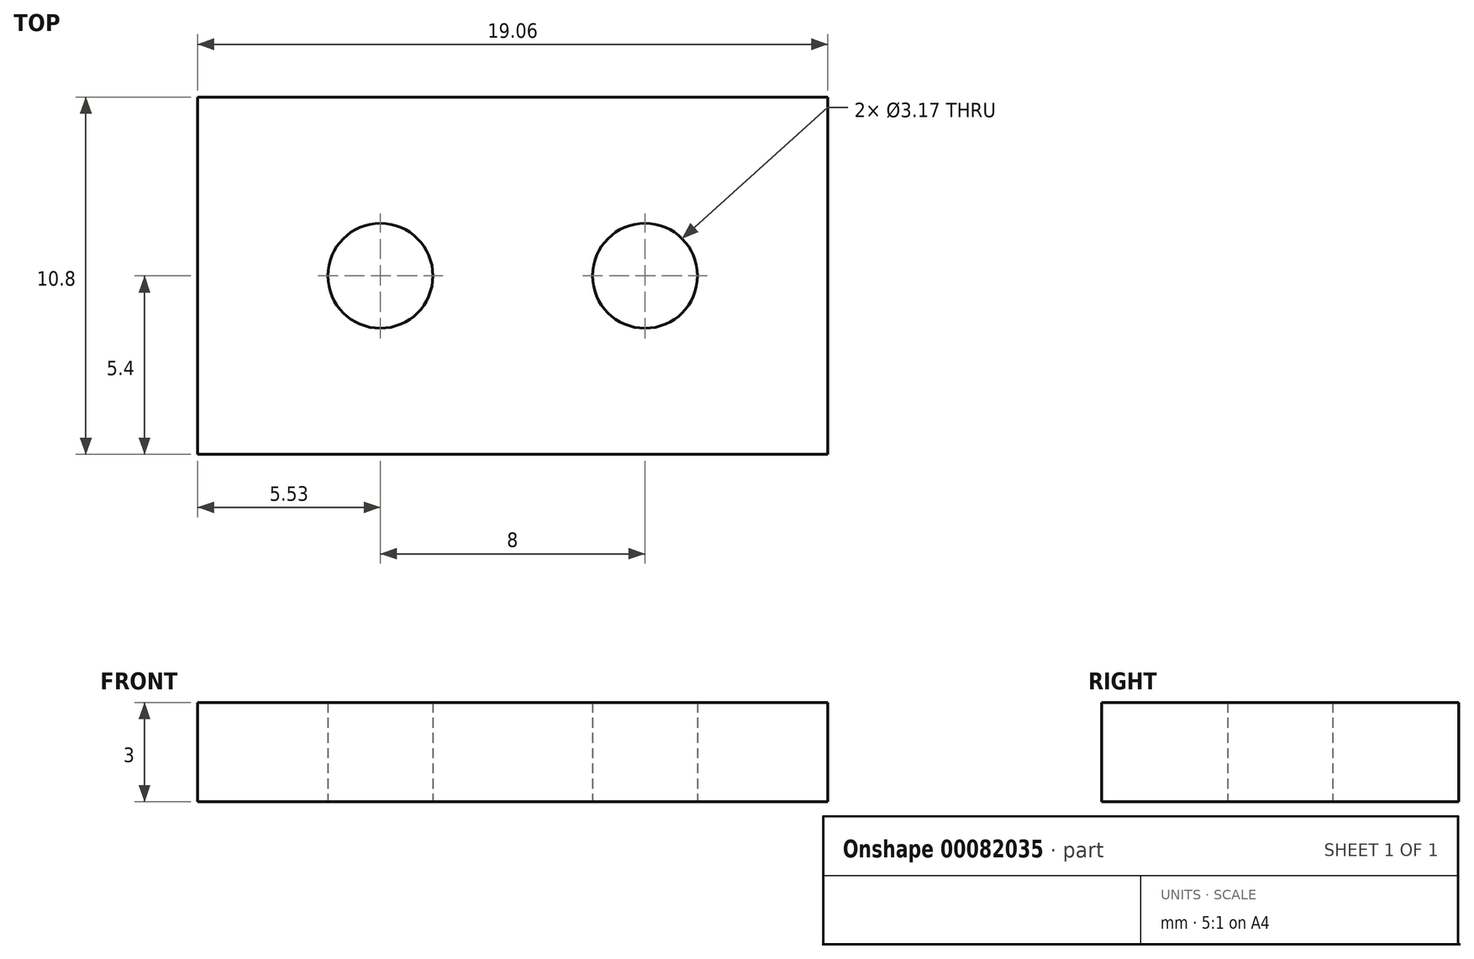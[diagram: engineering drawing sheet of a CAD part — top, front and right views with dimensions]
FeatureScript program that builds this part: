
annotation { "Feature Type Name" : "Feature", "Feature Type Description" : "" }
export const myFeature = defineFeature(function(context is Context, id is Id, definition is map)
    precondition{}
    {
        {
            var Q0;
            Q0=qCreatedBy(makeId("Top.planeOp"),FACE);
            var sketch = newSketch(context, id + "F0", { "sketchPlane" : qUnion([Q0])});
            skLineSegment(sketch, "E0.bottom", {"start": v(-9.53, 5.4) * mm, "end": v(9.53, 5.4) * mm});
            skLineSegment(sketch, "E0.top", {"start": v(-9.53, -5.4) * mm, "end": v(9.53, -5.4) * mm});
            skLineSegment(sketch, "E0.left", {"start": v(-9.53, 5.4) * mm, "end": v(-9.53, -5.4) * mm});
            skLineSegment(sketch, "E0.right", {"start": v(9.53, 5.4) * mm, "end": v(9.53, -5.4) * mm});
            skLineSegment(sketch, "E1", {"start": v(9.53, 5.4) * mm, "end": v(-9.53, -5.4) * mm, "construction": true});
            skCircle(sketch, "E2", {"center": v(-4, 0) * mm, "radius": 1.59 * mm});
            skCircle(sketch, "E3", {"center": v(4, 0) * mm, "radius": 1.59 * mm});
            skLineSegment(sketch, "E4", {"start": v(-4, 0) * mm, "end": v(4, 0) * mm, "construction": true});
            skSolve(sketch);
        }
        {
            var Q0;
            Q0 = qSketchRegion(id + "F0", true);
            extrude(context, id + "F1", {"entities" : qUnion([Q0]), "depth" : 3 * mm});
        }
    });
